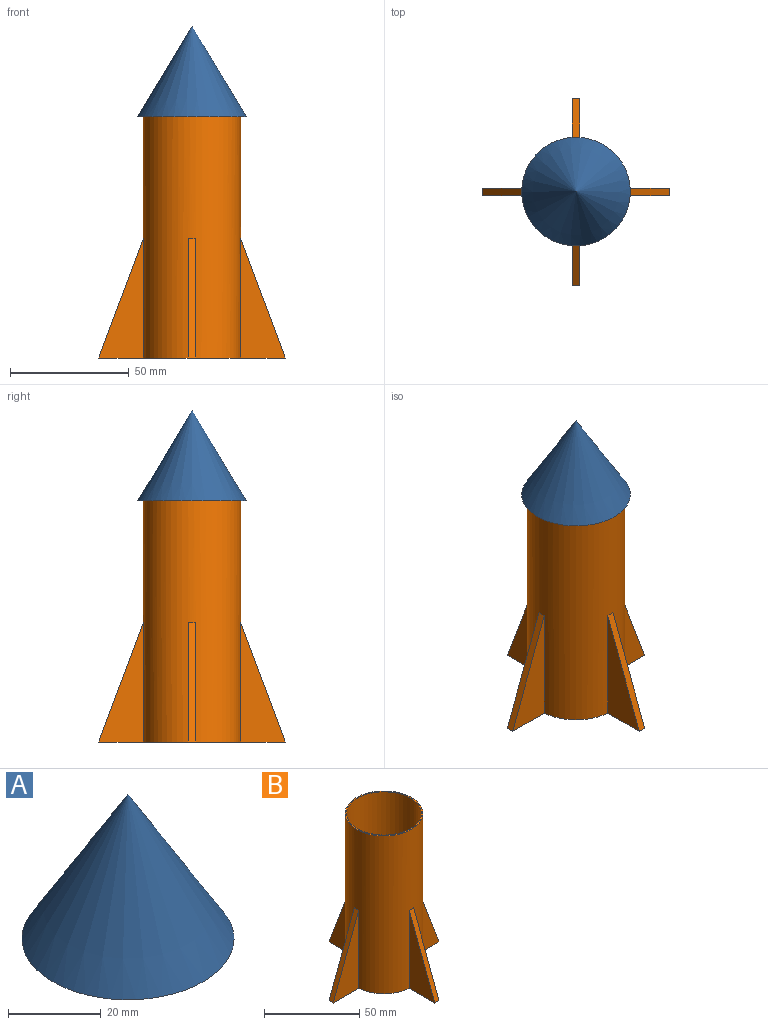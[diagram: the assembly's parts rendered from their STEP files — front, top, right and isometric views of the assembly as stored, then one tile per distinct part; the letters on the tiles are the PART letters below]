
ASSEMBLY  parts=2 mates=1
PART A: 9 faces, bbox 45.7x45.7x38.1 mm
  f0: plane 45.72x45.72mm, normal (0,0,-1), area 324.2mm2, adj f1,f2
  f1: cone r=0mm half-angle=31deg, axis (0,0,-1), area 3191mm2, adj f0
  f2: cylinder r=20.48mm len=40.96mm, axis (0,0,-1), area 204.3mm2, adj f0,f4
  f3: cylinder r=19.69mm len=39.37mm, axis (0,0,-1), area 196.3mm2, adj f4,f5
  f4: plane 40.96x40.96mm, normal (0,0,-1), area 100.2mm2, adj f2,f3
  f5: plane 39.37x39.37mm, normal (0,0,-1), area 152mm2, adj f3,f7
  f6: cone r=0mm half-angle=31deg, axis (0,0,-1), area 2361.2mm2, adj f8
  f7: cylinder r=18.41mm len=36.83mm, axis (0,0,-1), area 330.6mm2, adj f5,f8
  f8: plane 39.33x39.33mm, normal (0,0,1), area 149.5mm2, adj f6,f7
PART B: 16 faces, bbox 78.5x78.5x101.6 mm
  f0: cylinder r=20.48mm len=101.6mm, axis (0,0,-1), area 12435.2mm2, adj f2,f3,f4,f5,f6,f7,f8,f9
  f1: cylinder r=19.69mm len=101.6mm, axis (0,0,-1), area 12566.3mm2, adj f2,f3
  f2: plane 40.96x40.96mm, normal (0,0,1), area 100.2mm2, adj f0,f1
  f3: plane 78.55x78.55mm, normal (0,0,-1), area 339.1mm2, adj f0,f1,f4,f5,f6,f7,f8,f9
  f4: plane 50.29x18.86mm, normal (0,-1,0), area 474.1mm2, adj f0,f3,f6
  f5: plane 50.29x18.86mm, normal (0,1,0), area 474.1mm2, adj f0,f3,f6
  f6: plane 50.29x18.86mm, normal (0.94,0,0.35), area 170.1mm2, adj f0,f3,f4,f5
  f7: plane 50.29x18.86mm, normal (0,-1,0), area 474.1mm2, adj f0,f3,f9
  f8: plane 50.29x18.86mm, normal (0,1,0), area 474.1mm2, adj f0,f3,f9
  f9: plane 50.29x18.86mm, normal (-0.94,0,0.35), area 170.1mm2, adj f0,f3,f7,f8
  f10: plane 50.29x18.86mm, normal (1,0,0), area 474.1mm2, adj f0,f3,f12
  f11: plane 50.29x18.86mm, normal (-1,0,0), area 474.1mm2, adj f0,f3,f12
  f12: plane 50.29x18.86mm, normal (0,-0.94,0.35), area 170.1mm2, adj f0,f3,f10,f11
  f13: plane 50.29x18.86mm, normal (1,0,0), area 474.1mm2, adj f0,f3,f15
  f14: plane 50.29x18.86mm, normal (-1,0,0), area 474.1mm2, adj f0,f3,f15
  f15: plane 50.29x18.86mm, normal (0,0.94,0.35), area 170.1mm2, adj f0,f3,f13,f14
PLACE A t=(-106.64,-75.66,29.64)mm
PLACE B t=(-106.64,-75.66,-71.96)mm
MATE fastened A.f3 <-> B.f1  axis (0,0,-1) through (-106.64,-75.66,29.64)mm
